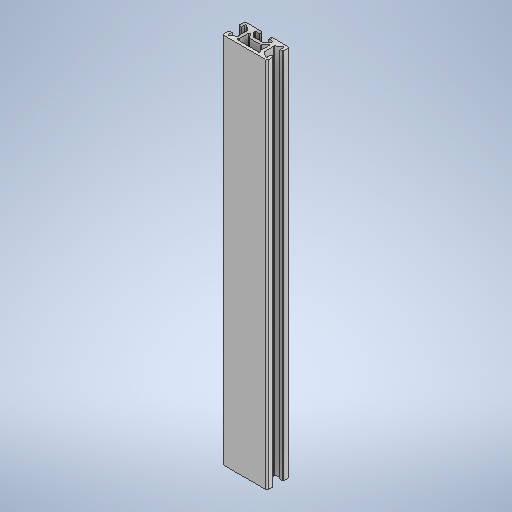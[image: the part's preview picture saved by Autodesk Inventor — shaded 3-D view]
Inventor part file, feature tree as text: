
AUTODESK INVENTOR PART (.ipt)
format: ipt  version: 2025.2 (Build 292293000, 293)  size: 398,848 bytes
history: native  units: mm
features: other x1, extrude x1, mirror x1, sketch x1
ambient origin geometry x8: Origin, YZ Plane, XZ Plane, XY Plane, X Axis, Y Axis, Z Axis, Center Point
bodies: Body1 (feature_tree)
feature tree (4):
  other  "Sólido1"
  extrude  "Extrusão1"  Depth=15.0mm
  mirror  "Espelhar1"
  sketch  "Esboço1"  dims[d14=30.0mm d15=15.0mm d22=2.0mm d23=0.5mm d34=2.5mm d35=1.0mm d37=0.5mm d38=8.726646mm d41=6.0mm d45=2.0mm d46=6.2mm d47=2.0mm d50=0.5mm d53=2.0mm d55=2.0mm d56=3.1mm d59=6.0mm d60=8.726646mm d62=2.0mm d64=1.465653mm d66=250.0mm d67=0.0mm d65=0.5mm d68=0.872665mm]
